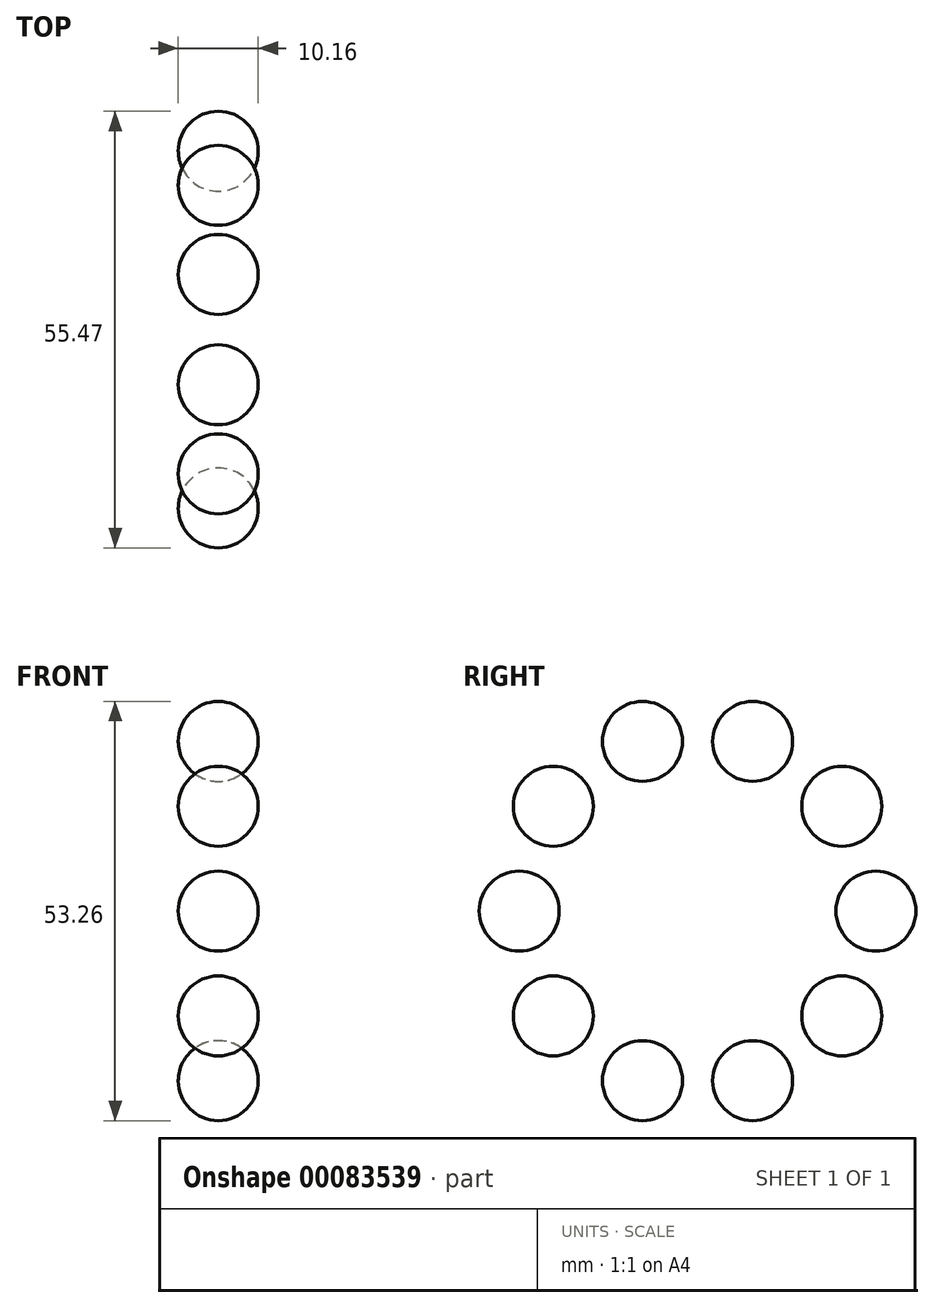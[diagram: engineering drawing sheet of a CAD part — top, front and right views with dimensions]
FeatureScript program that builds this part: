
annotation { "Feature Type Name" : "Feature", "Feature Type Description" : "" }
export const myFeature = defineFeature(function(context is Context, id is Id, definition is map)
    precondition{}
    {
        {
            var Q0;
            Q0=qCreatedBy(makeId("Front.planeOp"),FACE);
            var sketch = newSketch(context, id + "F0", { "sketchPlane" : qUnion([Q0])});
            skArc(sketch, "E0", {"start": v(5.08, 0) * mm, "mid": v(0, 5.08) * mm, "end": v(-5.08, 0) * mm});
            skLineSegment(sketch, "E1", {"start": v(-5.08, 0) * mm, "end": v(5.08, 0) * mm});
            skSolve(sketch);
        }
        {
            var Q0;
            Q0=makeQuery(id+"F0.imprint","IMPRINT",FACE,{"disambiguationData":[TD([[makeQuery(id+"F0.imprint","IMPRINT",EDGE,{"derivedFrom":sQuery(id+"F0.wireOp",EDGE,"E0")}),1.0]])]});
            var Q1;
            Q1=sQuery(id+"F0.wireOp",EDGE,"E1");
            revolve(context, id + "F1", {"entities" : qUnion([Q0]), "axis" : qUnion([Q1]), "revolveType" : RevolveType.FULL});
        }
        {
            var Q0;
            Q0=qCreatedBy(makeId("Top.planeOp"),FACE);
            var sketch = newSketch(context, id + "F2", { "sketchPlane" : qUnion([Q0])});
            skLineSegment(sketch, "E2", {"start": v(0, 0) * mm, "end": v(0, 22.66) * mm});
            skLineSegment(sketch, "E3", {"start": v(0, 22.66) * mm, "end": v(7, 22.66) * mm});
            skSolve(sketch);
        }
        {
            var Q0;
            Q0=makeQuery(id+"F1.opRevolve","SWEPT_BODY",BODY,{"disambiguationData":[OSD([sQuery(id+"F0.wireOp",EDGE,"E0"),sQuery(id+"F0.wireOp",EDGE,"E1")])]});
            var Q1;
            Q1=sQuery(id+"F2.wireOp",EDGE,"E3");
            circularPattern(context, id + "F3", {"entities" : qUnion([Q0]), "axis" : qUnion([Q1]), "angle" : 360 * degree, "instanceCount" : 10, "equalSpace" : true});
        }
    });
